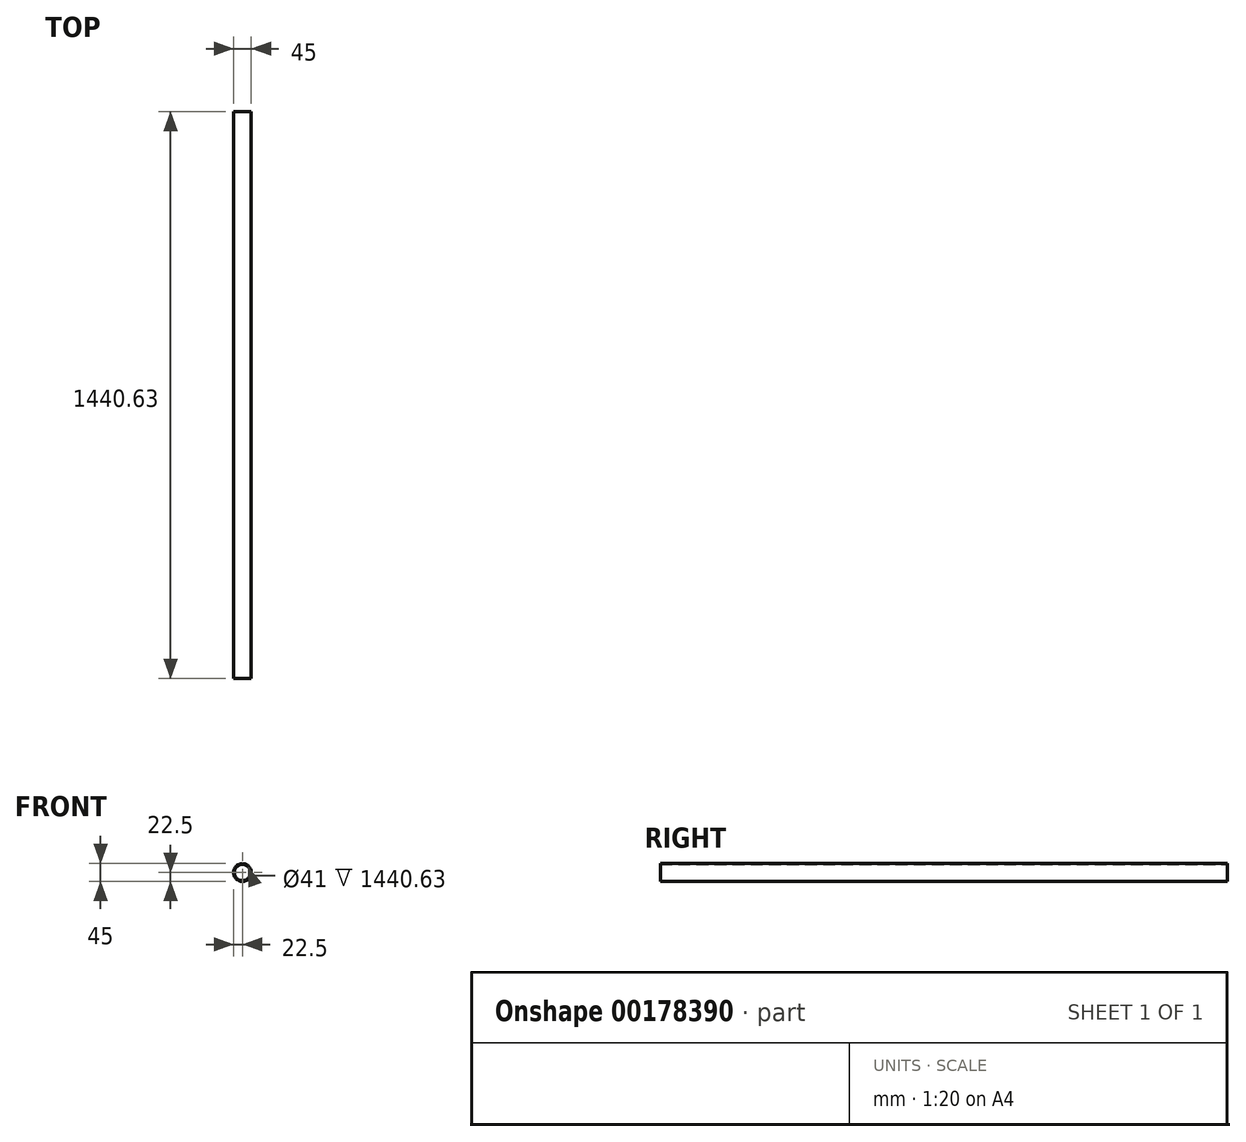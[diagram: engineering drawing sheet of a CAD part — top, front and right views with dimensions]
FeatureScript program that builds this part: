
annotation { "Feature Type Name" : "Feature", "Feature Type Description" : "" }
export const myFeature = defineFeature(function(context is Context, id is Id, definition is map)
    precondition{}
    {
        {
            var Q0;
            Q0=qCreatedBy(makeId("Front.planeOp"),FACE);
            var sketch = newSketch(context, id + "F0", { "sketchPlane" : qUnion([Q0])});
            skCircle(sketch, "E0", {"center": v(0, 0) * mm, "radius": 22.5 * mm});
            skCircle(sketch, "E1.0", {"center": v(0, 0) * mm, "radius": 20.5 * mm});
            skSolve(sketch);
        }
        {
            var Q0;
            Q0=makeQuery(id+"F0.imprint","IMPRINT",FACE,{"disambiguationData":[TD([[makeQuery(id+"F0.imprint","IMPRINT",EDGE,{"derivedFrom":sQuery(id+"F0.wireOp",EDGE,"E0")}),1.0]])]});
            extrude(context, id + "F1", {"entities" : qUnion([Q0]), "depth" : 1440.63 * mm});
        }
    });
